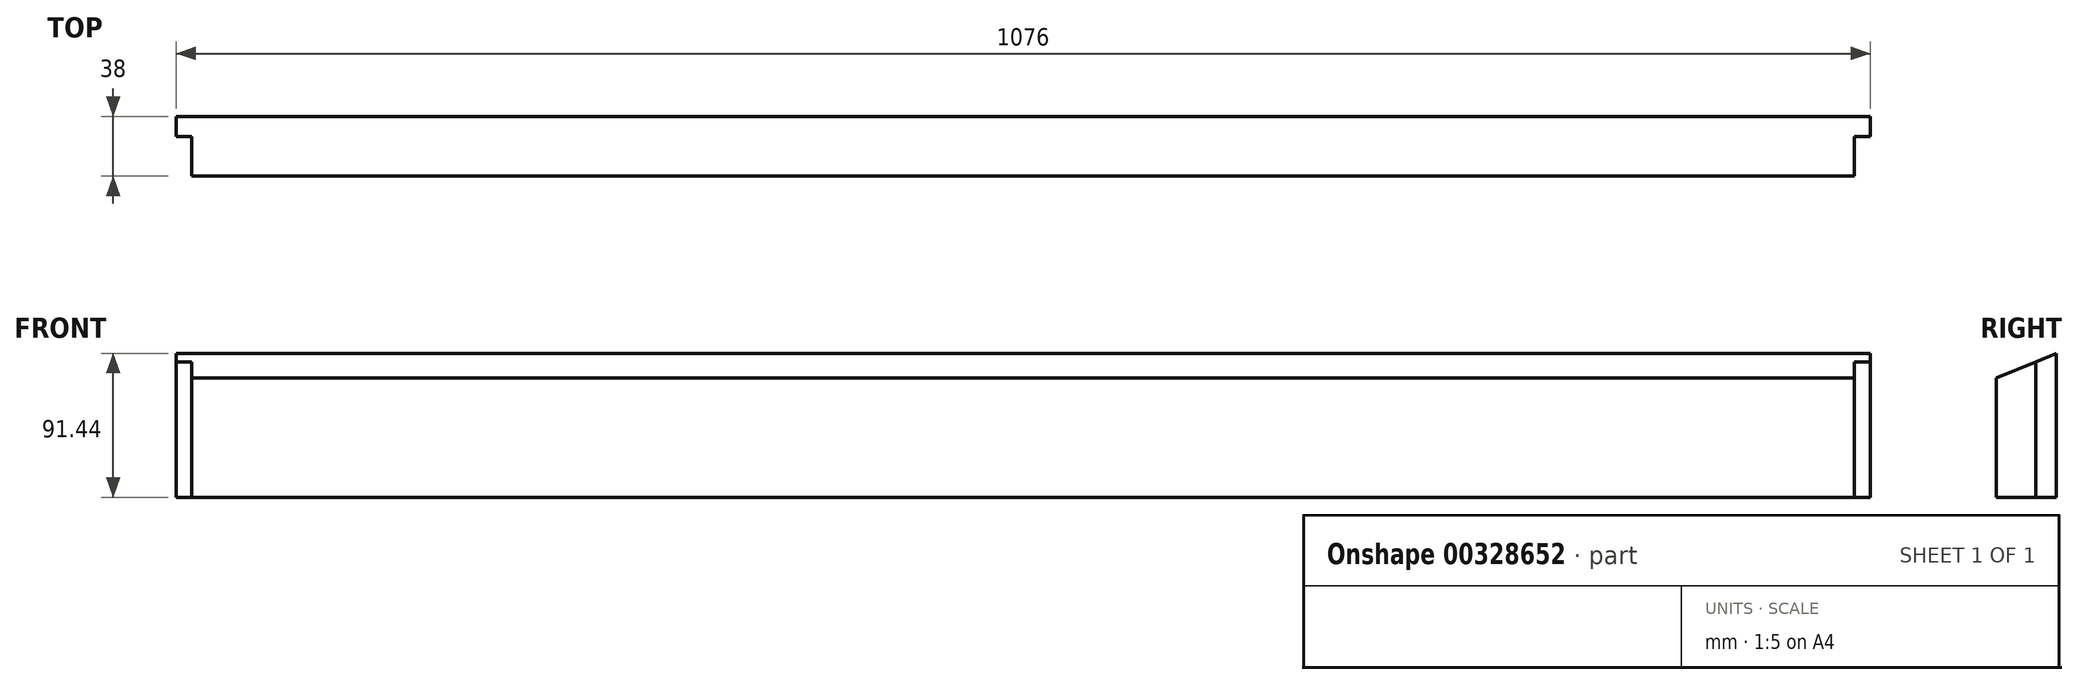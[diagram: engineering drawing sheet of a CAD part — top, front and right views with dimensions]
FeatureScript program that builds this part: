
annotation { "Feature Type Name" : "Feature", "Feature Type Description" : "" }
export const myFeature = defineFeature(function(context is Context, id is Id, definition is map)
    precondition{}
    {
        {
            var Q0;
            Q0=qCreatedBy(makeId("Right.planeOp"),FACE);
            var sketch = newSketch(context, id + "F0", { "sketchPlane" : qUnion([Q0])});
            skLineSegment(sketch, "E0.bottom", {"start": v(0, 0) * mm, "end": v(38, 0) * mm});
            skLineSegment(sketch, "E0.left", {"start": v(0, 0) * mm, "end": v(0, 75.7) * mm});
            skLineSegment(sketch, "E1", {"start": v(38, 0) * mm, "end": v(38, 91.44) * mm});
            skLineSegment(sketch, "E2", {"start": v(38, 91.44) * mm, "end": v(0, 75.7) * mm});
            skSolve(sketch);
        }
        {
            var Q0;
            Q0=qSketchRegion(id+"F0",true);
            extrude(context, id + "F1", {"entities" : qUnion([Q0]), "oppositeDirection" : true, "depth" : 1056 * mm});
        }
        {
            var Q0;
            Q0=makeQuery(id+"F1.opExtrude","CAP_FACE",FACE,{"disambiguationData":[OSD([sQuery(id+"F0.wireOp",EDGE,"E0.bottom"),sQuery(id+"F0.wireOp",EDGE,"E0.left"),sQuery(id+"F0.wireOp",EDGE,"E1"),sQuery(id+"F0.wireOp",EDGE,"E2")])],"isStart":true});
            var sketch = newSketch(context, id + "F2", { "sketchPlane" : qUnion([Q0])});
            skLineSegment(sketch, "E3", {"start": v(25, 0) * mm, "end": v(25, 86.06) * mm});
            skLineSegment(sketch, "E4", {"start": v(25, 86.06) * mm, "end": v(38, 91.44) * mm});
            skLineSegment(sketch, "E5", {"start": v(38, 91.44) * mm, "end": v(38, 0) * mm});
            skLineSegment(sketch, "E6", {"start": v(38, 0) * mm, "end": v(25, 0) * mm});
            skSolve(sketch);
        }
        {
            var Q0;
            Q0=qSketchRegion(id+"F2",true);
            extrude(context, id + "F3", {"entities" : qUnion([Q0]), "operationType" : NewBodyOperationType.ADD, "depth" : 10 * mm});
        }
        {
            var Q0;
            Q0=makeQuery(id+"F1.opExtrude","CAP_FACE",FACE,{"disambiguationData":[OSD([sQuery(id+"F0.wireOp",EDGE,"E0.bottom"),sQuery(id+"F0.wireOp",EDGE,"E0.left"),sQuery(id+"F0.wireOp",EDGE,"E1"),sQuery(id+"F0.wireOp",EDGE,"E2")])],"isStart":false});
            var sketch = newSketch(context, id + "F4", { "sketchPlane" : qUnion([Q0])});
            skLineSegment(sketch, "E7", {"start": v(-25, 0) * mm, "end": v(-25, 86.06) * mm});
            skLineSegment(sketch, "E8", {"start": v(-25, 86.06) * mm, "end": v(-38, 91.44) * mm});
            skLineSegment(sketch, "E9", {"start": v(-38, 91.44) * mm, "end": v(-38, 0) * mm});
            skLineSegment(sketch, "E10", {"start": v(-38, 0) * mm, "end": v(-25, 0) * mm});
            skSolve(sketch);
        }
        {
            var Q0;
            Q0=qSketchRegion(id+"F4",true);
            extrude(context, id + "F5", {"entities" : qUnion([Q0]), "operationType" : NewBodyOperationType.ADD, "depth" : 10 * mm});
        }
    });
